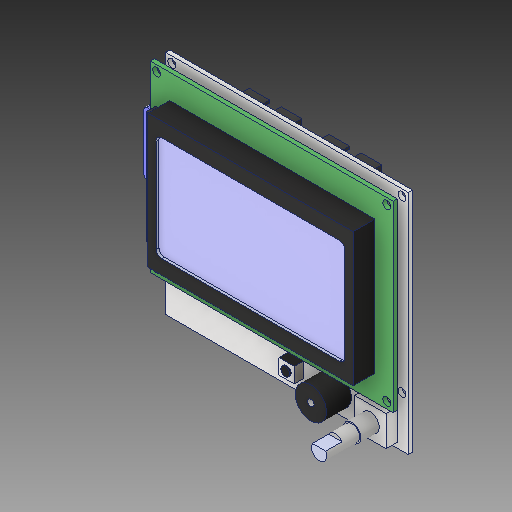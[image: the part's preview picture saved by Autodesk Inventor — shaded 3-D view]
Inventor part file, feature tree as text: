
AUTODESK INVENTOR PART (.ipt)
format: ipt  version: 2018 (Build 220112000, 112)  size: 208,896 bytes
history: native  units: mm
features: fillet x1
ambient origin geometry x8: Origin, YZ Plane, XZ Plane, XY Plane, X Axis, Y Axis, Z Axis, Center Point
bodies: Solid1 (feature_tree)
feature tree (1):
  fillet  "Fillet1 - SD Card"  [1 undecoded]
note: 1 required parameter value undecoded (feature->parameter linkage not recoverable at this tier; creation-order binding heuristic only, values carry confidence <= 0.55)
